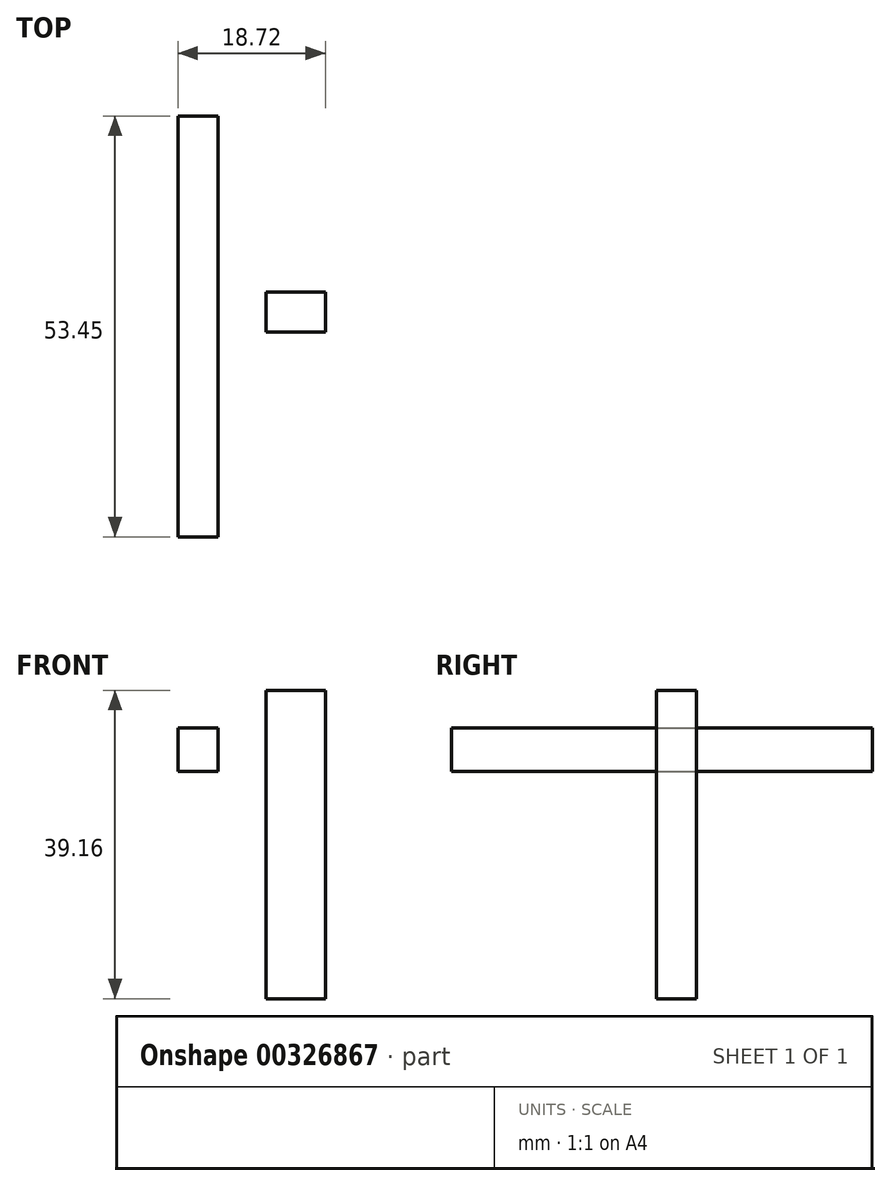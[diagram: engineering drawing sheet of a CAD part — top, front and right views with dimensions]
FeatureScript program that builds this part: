
annotation { "Feature Type Name" : "Feature", "Feature Type Description" : "" }
export const myFeature = defineFeature(function(context is Context, id is Id, definition is map)
    precondition{}
    {
        {
            var Q0;
            Q0=qCreatedBy(makeId("Right.planeOp"),FACE);
            var sketch = newSketch(context, id + "F0", { "sketchPlane" : qUnion([Q0])});
            skLineSegment(sketch, "E0.bottom", {"start": v(-31.12, 34.41) * mm, "end": v(22.33, 34.41) * mm});
            skLineSegment(sketch, "E0.top", {"start": v(-31.12, 28.84) * mm, "end": v(22.33, 28.84) * mm});
            skLineSegment(sketch, "E0.left", {"start": v(-31.12, 34.41) * mm, "end": v(-31.12, 28.84) * mm});
            skLineSegment(sketch, "E0.right", {"start": v(22.33, 34.41) * mm, "end": v(22.33, 28.84) * mm});
            skSolve(sketch);
        }
        {
            var Q0;
            Q0 = qSketchRegion(id + "F0", true);
            extrude(context, id + "F1", {"entities" : qUnion([Q0]), "depth" : 5.08 * mm});
        }
        {
            var Q0;
            Q0=qCreatedBy(makeId("Front.planeOp"),FACE);
            var sketch = newSketch(context, id + "F2", { "sketchPlane" : qUnion([Q0])});
            skLineSegment(sketch, "E1.bottom", {"start": v(18.72, 39.16) * mm, "end": v(11.19, 39.16) * mm});
            skLineSegment(sketch, "E1.top", {"start": v(18.72, 0) * mm, "end": v(11.19, 0) * mm});
            skLineSegment(sketch, "E1.left", {"start": v(18.72, 39.16) * mm, "end": v(18.72, 0) * mm});
            skLineSegment(sketch, "E1.right", {"start": v(11.19, 39.16) * mm, "end": v(11.19, 0) * mm});
            skSolve(sketch);
        }
        {
            var Q0;
            Q0=makeQuery(id+"F2.imprint","IMPRINT",FACE,{"disambiguationData":[TD([[makeQuery(id+"F2.imprint","IMPRINT",EDGE,{"derivedFrom":sQuery(id+"F2.wireOp",EDGE,"E1.bottom")}),1.0]])]});
            extrude(context, id + "F3", {"entities" : qUnion([Q0]), "depth" : 5.08 * mm});
        }
    });
